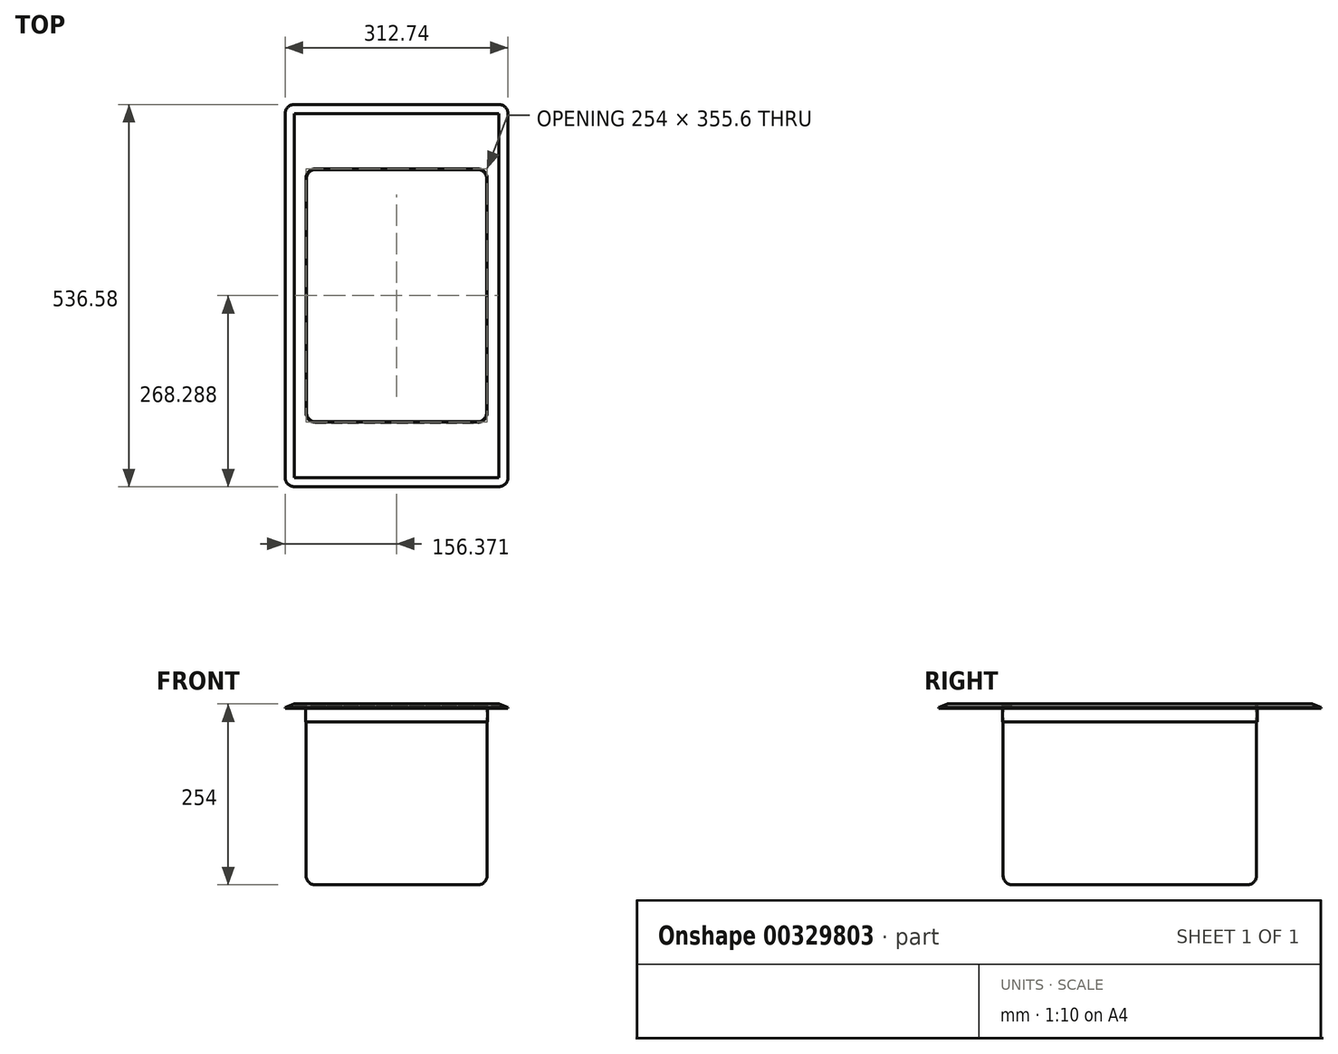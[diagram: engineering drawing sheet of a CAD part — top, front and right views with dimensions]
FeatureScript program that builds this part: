
annotation { "Feature Type Name" : "Feature", "Feature Type Description" : "" }
export const myFeature = defineFeature(function(context is Context, id is Id, definition is map)
    precondition{}
    {
        {
            var Q0;
            Q0=qCreatedBy(makeId("Top.planeOp"),FACE);
            var sketch = newSketch(context, id + "F0", { "sketchPlane" : qUnion([Q0])});
            skLineSegment(sketch, "E0.bottom", {"start": v(-12.7, 0) * mm, "end": v(-300.04, 0) * mm});
            skLineSegment(sketch, "E0.top", {"start": v(-12.7, 536.58) * mm, "end": v(-300.04, 536.58) * mm});
            skLineSegment(sketch, "E0.left", {"start": v(0, 12.7) * mm, "end": v(0, 523.88) * mm});
            skLineSegment(sketch, "E0.right", {"start": v(-312.74, 12.7) * mm, "end": v(-312.74, 523.88) * mm});
            skLineSegment(sketch, "E1.bottom", {"start": v(-270.67, 446.09) * mm, "end": v(-42.07, 446.09) * mm});
            skLineSegment(sketch, "E1.top", {"start": v(-270.67, 90.49) * mm, "end": v(-42.07, 90.49) * mm});
            skLineSegment(sketch, "E1.left", {"start": v(-283.37, 433.39) * mm, "end": v(-283.37, 103.19) * mm});
            skLineSegment(sketch, "E1.right", {"start": v(-29.37, 433.39) * mm, "end": v(-29.37, 103.19) * mm});
            skPoint(sketch, "E2.visualSharp", {"position": v(-29.37, 446.09) * mm});
            skArc(sketch, "E2.filletArc", {"start": v(-29.37, 433.39) * mm, "mid": v(-33.09, 442.37) * mm, "end": v(-42.07, 446.09) * mm});
            skPoint(sketch, "E3.visualSharp", {"position": v(-283.37, 446.09) * mm});
            skArc(sketch, "E3.filletArc", {"start": v(-270.67, 446.09) * mm, "mid": v(-279.65, 442.37) * mm, "end": v(-283.37, 433.39) * mm});
            skPoint(sketch, "E4.visualSharp", {"position": v(-283.37, 90.49) * mm});
            skArc(sketch, "E4.filletArc", {"start": v(-283.37, 103.19) * mm, "mid": v(-279.65, 94.2) * mm, "end": v(-270.67, 90.49) * mm});
            skPoint(sketch, "E5.visualSharp", {"position": v(-29.37, 90.49) * mm});
            skArc(sketch, "E5.filletArc", {"start": v(-42.07, 90.49) * mm, "mid": v(-33.09, 94.2) * mm, "end": v(-29.37, 103.19) * mm});
            skPoint(sketch, "E6.visualSharp", {"position": v(0, 536.58) * mm});
            skArc(sketch, "E6.filletArc", {"start": v(0, 523.88) * mm, "mid": v(-3.72, 532.86) * mm, "end": v(-12.7, 536.58) * mm});
            skPoint(sketch, "E7.visualSharp", {"position": v(-312.74, 536.58) * mm});
            skArc(sketch, "E7.filletArc", {"start": v(-300.04, 536.58) * mm, "mid": v(-309.02, 532.86) * mm, "end": v(-312.74, 523.88) * mm});
            skPoint(sketch, "E8.visualSharp", {"position": v(-312.74, 0) * mm});
            skArc(sketch, "E8.filletArc", {"start": v(-312.74, 12.7) * mm, "mid": v(-309.02, 3.72) * mm, "end": v(-300.04, 0) * mm});
            skPoint(sketch, "E9.visualSharp", {"position": v(0, 0) * mm});
            skArc(sketch, "E9.filletArc", {"start": v(-12.7, 0) * mm, "mid": v(-3.72, 3.72) * mm, "end": v(0, 12.7) * mm});
            skSolve(sketch);
        }
        {
            var Q0;
            Q0=makeQuery(id+"F0.imprint","IMPRINT",FACE,{"disambiguationData":[TD([[makeQuery(id+"F0.imprint","IMPRINT",EDGE,{"derivedFrom":sQuery(id+"F0.wireOp",EDGE,"E1.bottom")}),-1.0]])]});
            extrude(context, id + "F1", {"entities" : qUnion([Q0]), "oppositeDirection" : true, "depth" : 254 * mm});
        }
        {
            var Q0;
            Q0=makeQuery(id+"F1.opExtrude","CAP_FACE",FACE,{"disambiguationData":[OSD([sQuery(id+"F0.wireOp",EDGE,"E1.bottom"),sQuery(id+"F0.wireOp",EDGE,"E1.top"),sQuery(id+"F0.wireOp",EDGE,"E1.left"),sQuery(id+"F0.wireOp",EDGE,"E1.right"),sQuery(id+"F0.wireOp",EDGE,"E2.filletArc"),sQuery(id+"F0.wireOp",EDGE,"E3.filletArc"),sQuery(id+"F0.wireOp",EDGE,"E4.filletArc"),sQuery(id+"F0.wireOp",EDGE,"E5.filletArc")])],"isStart":false});
            fillet(context, id + "F2", {"entities" : qUnion([Q0]), "radius" : 12.7 * mm, "tangentPropagation" : true, "allowEdgeOverflow" : false});
        }
        {
            var Q0;
            Q0=makeQuery(id+"F1.opExtrude","CAP_FACE",FACE,{"disambiguationData":[OSD([sQuery(id+"F0.wireOp",EDGE,"E1.bottom"),sQuery(id+"F0.wireOp",EDGE,"E1.top"),sQuery(id+"F0.wireOp",EDGE,"E1.left"),sQuery(id+"F0.wireOp",EDGE,"E1.right"),sQuery(id+"F0.wireOp",EDGE,"E2.filletArc"),sQuery(id+"F0.wireOp",EDGE,"E3.filletArc"),sQuery(id+"F0.wireOp",EDGE,"E4.filletArc"),sQuery(id+"F0.wireOp",EDGE,"E5.filletArc")])],"isStart":true});
            shell(context, id + "F3", {"entities" : qUnion([Q0]), "thickness" : 0.89 * mm});
        }
        {
            var Q0;
            Q0=makeQuery(id+"F0.imprint","IMPRINT",FACE,{"disambiguationData":[TD([[makeQuery(id+"F0.imprint","IMPRINT",EDGE,{"derivedFrom":sQuery(id+"F0.wireOp",EDGE,"E0.bottom")}),-1.0]])]});
            extrude(context, id + "F4", {"entities" : qUnion([Q0]), "oppositeDirection" : true, "depth" : 25.4 * mm});
        }
        {
            var Q0;
            Q0=makeQuery(id+"F4.opExtrude","CAP_EDGE",EDGE,{"disambiguationData":[OSD([sQuery(id+"F0.wireOp",EDGE,"E0.right")])],"isStart":true});
            chamfer(context, id + "F5", {"entities" : qUnion([Q0]), "chamferType" : ChamferType.TWO_OFFSETS, "width1" : 5.08 * mm, "oppositeDirection" : false, "width2" : 12.7 * mm, "tangentPropagation" : true});
        }
        {
            var Q0;
            Q0=makeQuery(id+"F4.opExtrude","CAP_FACE",FACE,{"disambiguationData":[OSD([sQuery(id+"F0.wireOp",EDGE,"E0.bottom"),sQuery(id+"F0.wireOp",EDGE,"E0.top"),sQuery(id+"F0.wireOp",EDGE,"E0.left"),sQuery(id+"F0.wireOp",EDGE,"E0.right"),sQuery(id+"F0.wireOp",EDGE,"E1.bottom"),sQuery(id+"F0.wireOp",EDGE,"E1.top"),sQuery(id+"F0.wireOp",EDGE,"E1.left"),sQuery(id+"F0.wireOp",EDGE,"E1.right"),sQuery(id+"F0.wireOp",EDGE,"E2.filletArc"),sQuery(id+"F0.wireOp",EDGE,"E3.filletArc"),sQuery(id+"F0.wireOp",EDGE,"E4.filletArc"),sQuery(id+"F0.wireOp",EDGE,"E5.filletArc"),sQuery(id+"F0.wireOp",EDGE,"E6.filletArc"),sQuery(id+"F0.wireOp",EDGE,"E7.filletArc"),sQuery(id+"F0.wireOp",EDGE,"E8.filletArc"),sQuery(id+"F0.wireOp",EDGE,"E9.filletArc")])],"isStart":false});
            var Q1;
            Q1=makeQuery(id+"F4.opExtrude","SWEPT_FACE",FACE,{"disambiguationData":[OSD([sQuery(id+"F0.wireOp",EDGE,"E0.bottom")])]});
            var Q2;
            Q2=makeQuery(id+"F4.opExtrude","SWEPT_FACE",FACE,{"disambiguationData":[OSD([sQuery(id+"F0.wireOp",EDGE,"E0.left")])]});
            var Q3;
            Q3=makeQuery(id+"F4.opExtrude","SWEPT_FACE",FACE,{"disambiguationData":[OSD([sQuery(id+"F0.wireOp",EDGE,"E9.filletArc")])]});
            var Q4;
            Q4=makeQuery(id+"F4.opExtrude","SWEPT_FACE",FACE,{"disambiguationData":[OSD([sQuery(id+"F0.wireOp",EDGE,"E8.filletArc")])]});
            var Q5;
            Q5=makeQuery(id+"F4.opExtrude","SWEPT_FACE",FACE,{"disambiguationData":[OSD([sQuery(id+"F0.wireOp",EDGE,"E0.right")])]});
            var Q6;
            Q6=makeQuery(id+"F4.opExtrude","SWEPT_FACE",FACE,{"disambiguationData":[OSD([sQuery(id+"F0.wireOp",EDGE,"E7.filletArc")])]});
            var Q7;
            Q7=makeQuery(id+"F4.opExtrude","SWEPT_FACE",FACE,{"disambiguationData":[OSD([sQuery(id+"F0.wireOp",EDGE,"E0.top")])]});
            var Q8;
            Q8=makeQuery(id+"F4.opExtrude","SWEPT_FACE",FACE,{"disambiguationData":[OSD([sQuery(id+"F0.wireOp",EDGE,"E6.filletArc")])]});
            shell(context, id + "F6", {"entities" : qUnion([Q0, Q1, Q2, Q3, Q4, Q5, Q6, Q7, Q8]), "thickness" : 0.89 * mm});
        }
    });
